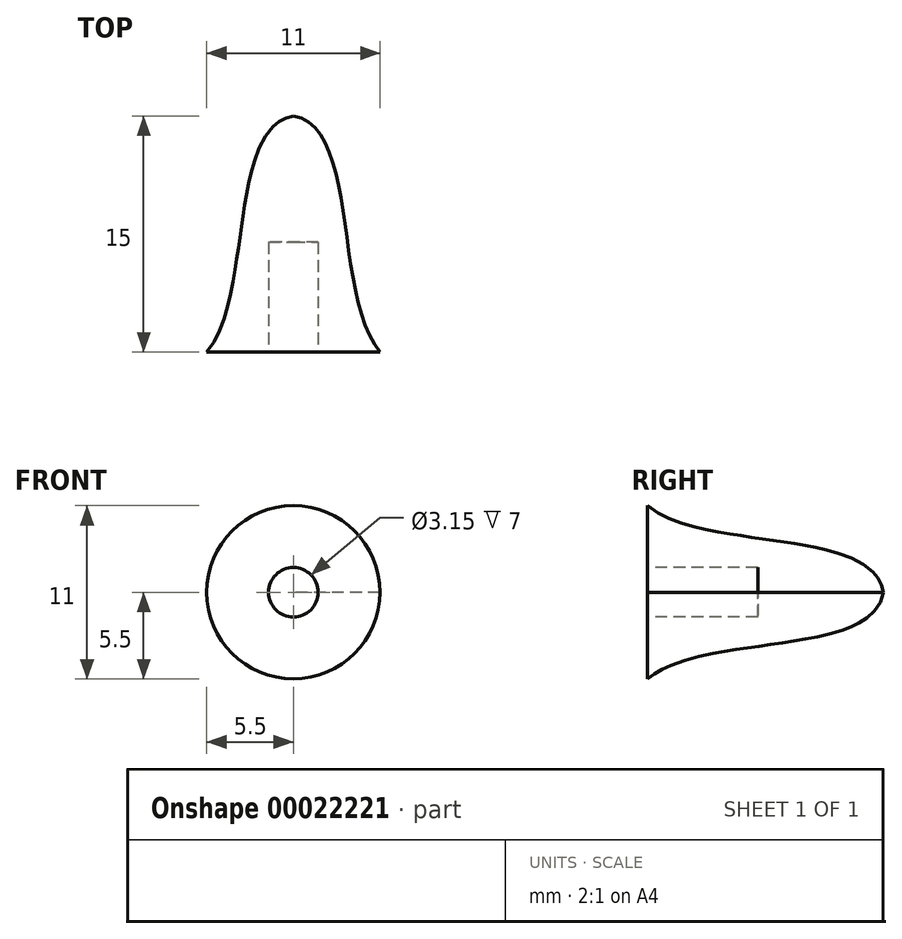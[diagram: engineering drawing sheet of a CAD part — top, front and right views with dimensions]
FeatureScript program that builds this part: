
annotation { "Feature Type Name" : "Feature", "Feature Type Description" : "" }
export const myFeature = defineFeature(function(context is Context, id is Id, definition is map)
    precondition{}
    {
        {
            var Q0;
            Q0=qCreatedBy(makeId("Top.planeOp"),FACE);
            var sketch = newSketch(context, id + "F0", { "sketchPlane" : qUnion([Q0])});
            skLineSegment(sketch, "E0.bottom", {"start": v(1.57, 0) * mm, "end": v(5.5, 0) * mm});
            skLineSegment(sketch, "E0.left", {"start": v(0, 7) * mm, "end": v(0, 15) * mm});
            skFitSpline(sketch, "E1", {"points": [v(5.5, 0) * mm, v(0, 15) * mm], "startDerivative": vector(-8.91, 10.74) * mm, "endDerivative": vector(-12.6, 2.05) * mm});
            skLineSegment(sketch, "E2.top", {"start": v(0, 7) * mm, "end": v(1.57, 7) * mm});
            skLineSegment(sketch, "E2.right", {"start": v(1.57, 0) * mm, "end": v(1.57, 7) * mm});
            skSolve(sketch);
        }
        {
            var Q0;
            Q0=qSketchRegion(id+"F0",true);
            var Q1;
            Q1=sQuery(id+"F0.wireOp",EDGE,"E0.left");
            revolve(context, id + "F1", {"entities" : qUnion([Q0]), "axis" : qUnion([Q1]), "revolveType" : RevolveType.FULL});
        }
    });
